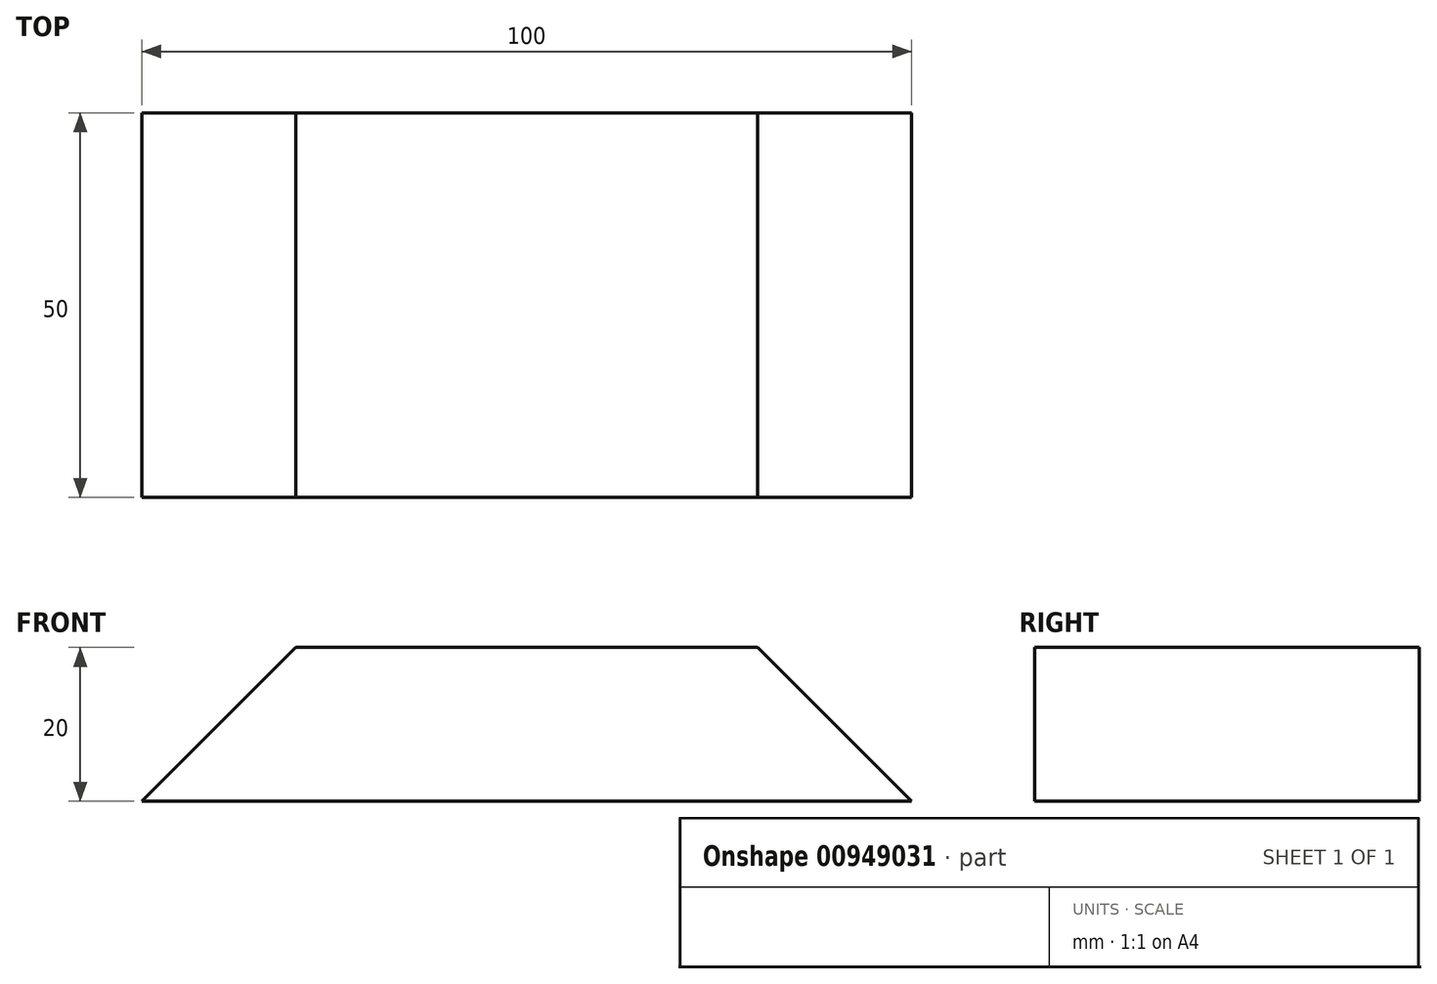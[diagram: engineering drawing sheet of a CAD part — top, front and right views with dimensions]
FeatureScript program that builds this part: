
annotation { "Feature Type Name" : "Feature", "Feature Type Description" : "" }
export const myFeature = defineFeature(function(context is Context, id is Id, definition is map)
    precondition{}
    {
        {
            var Q0;
            Q0=qCreatedBy(makeId("Front.planeOp"),FACE);
            var sketch = newSketch(context, id + "F0", { "sketchPlane" : qUnion([Q0])});
            skLineSegment(sketch, "E0.bottom", {"start": v(-31.55, -11.84) * mm, "end": v(68.45, -11.84) * mm});
            skLineSegment(sketch, "E0.top", {"start": v(-11.55, 8.16) * mm, "end": v(48.45, 8.16) * mm});
            skLineSegment(sketch, "E1", {"start": v(-31.55, -11.84) * mm, "end": v(-11.55, 8.16) * mm});
            skLineSegment(sketch, "E2", {"start": v(68.45, -11.84) * mm, "end": v(48.45, 8.16) * mm});
            skSolve(sketch);
        }
        {
            var Q0;
            Q0=makeQuery(id+"F0.imprint","IMPRINT",FACE,{"disambiguationData":[TD([[makeQuery(id+"F0.imprint","IMPRINT",EDGE,{"derivedFrom":sQuery(id+"F0.wireOp",EDGE,"E0.bottom")}),1.0]])]});
            extrude(context, id + "F1", {"entities" : qUnion([Q0]), "depth" : 50 * mm, "offsetDistance" : 25 * mm});
        }
    });
